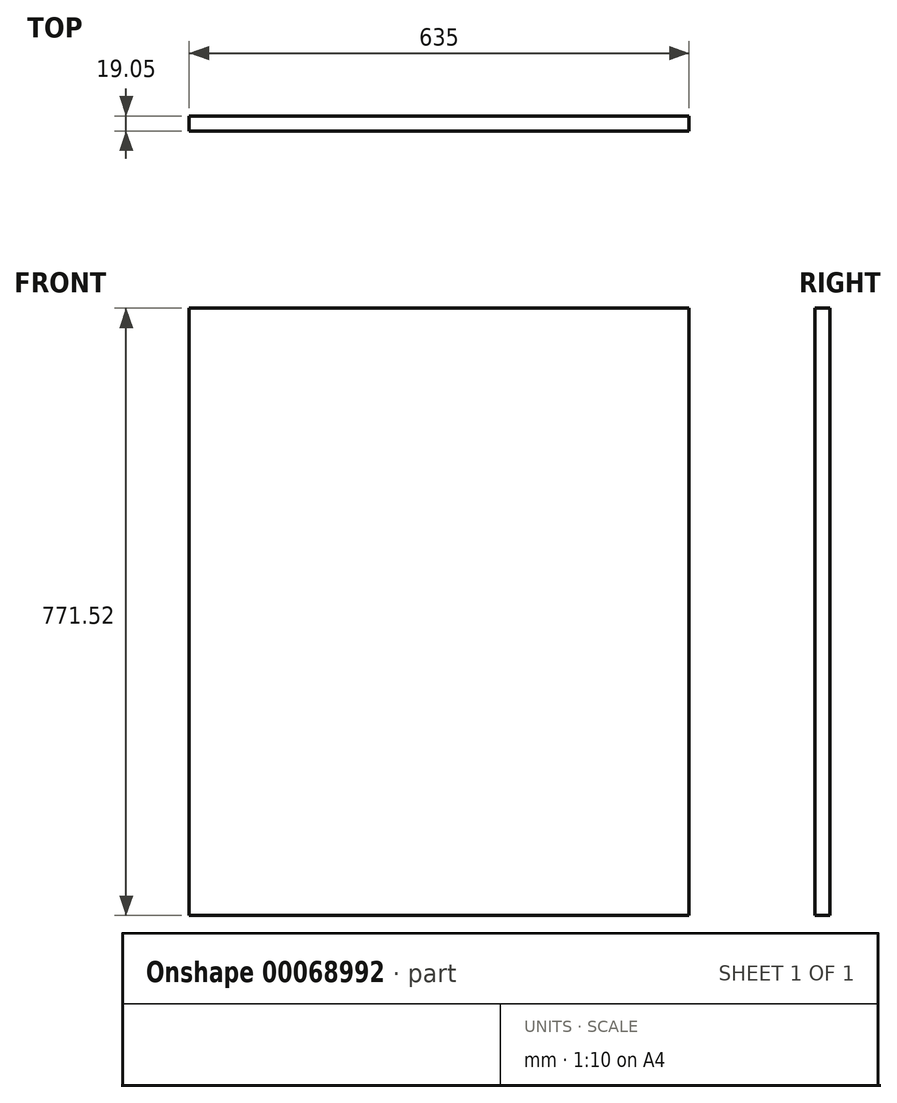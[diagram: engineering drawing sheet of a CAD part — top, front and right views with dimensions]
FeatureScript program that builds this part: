
annotation { "Feature Type Name" : "Feature", "Feature Type Description" : "" }
export const myFeature = defineFeature(function(context is Context, id is Id, definition is map)
    precondition{}
    {
        {
            var Q0;
            Q0=qCreatedBy(makeId("Front.planeOp"),FACE);
            var sketch = newSketch(context, id + "F0", { "sketchPlane" : qUnion([Q0])});
            skLineSegment(sketch, "E0.bottom", {"start": v(0, 0) * mm, "end": v(635, 0) * mm});
            skLineSegment(sketch, "E0.top", {"start": v(0, 771.53) * mm, "end": v(635, 771.53) * mm});
            skLineSegment(sketch, "E0.left", {"start": v(0, 0) * mm, "end": v(0, 771.53) * mm});
            skLineSegment(sketch, "E0.right", {"start": v(635, 0) * mm, "end": v(635, 771.53) * mm});
            skSolve(sketch);
        }
        {
            var Q0;
            Q0=makeQuery(id+"F0.imprint","IMPRINT",FACE,{"disambiguationData":[TD([[makeQuery(id+"F0.imprint","IMPRINT",EDGE,{"derivedFrom":sQuery(id+"F0.wireOp",EDGE,"E0.bottom")}),1.0]])]});
            extrude(context, id + "F1", {"entities" : qUnion([Q0]), "depth" : 19.05 * mm});
        }
    });
